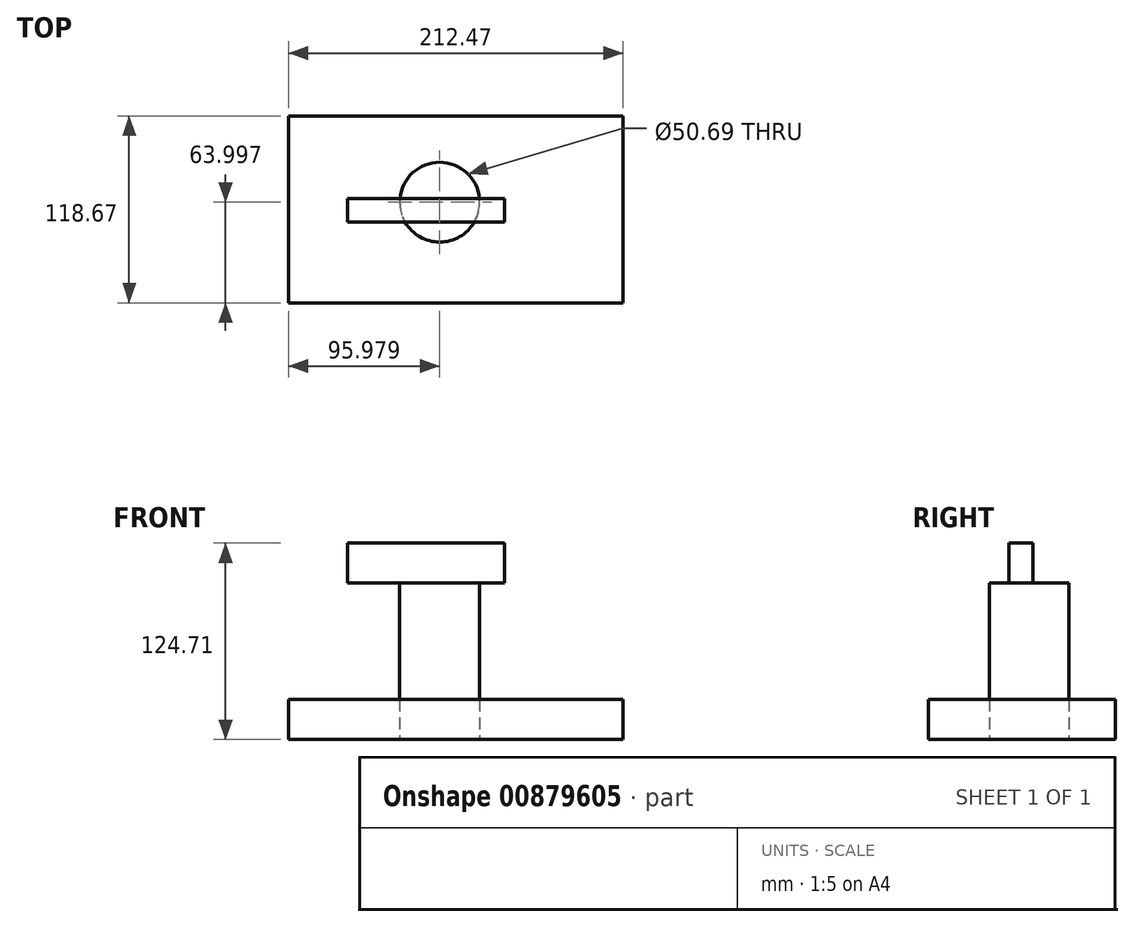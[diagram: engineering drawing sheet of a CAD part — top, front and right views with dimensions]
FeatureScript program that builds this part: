
annotation { "Feature Type Name" : "Feature", "Feature Type Description" : "" }
export const myFeature = defineFeature(function(context is Context, id is Id, definition is map)
    precondition{}
    {
        {
            var Q0;
            Q0=qCreatedBy(makeId("Top.planeOp"),FACE);
            var sketch = newSketch(context, id + "F0", { "sketchPlane" : qUnion([Q0])});
            skLineSegment(sketch, "E0.bottom", {"start": v(-143.27, 59.79) * mm, "end": v(69.2, 59.79) * mm});
            skLineSegment(sketch, "E0.top", {"start": v(-143.27, -58.88) * mm, "end": v(69.2, -58.88) * mm});
            skLineSegment(sketch, "E0.left", {"start": v(-143.27, 59.79) * mm, "end": v(-143.27, -58.88) * mm});
            skLineSegment(sketch, "E0.right", {"start": v(69.2, 59.79) * mm, "end": v(69.2, -58.88) * mm});
            skCircle(sketch, "E1", {"center": v(-47.3, 5.12) * mm, "radius": 25.35 * mm});
            skSolve(sketch);
        }
        {
            var Q0;
            Q0=makeQuery(id+"F0.imprint","IMPRINT",FACE,{"disambiguationData":[TD([[makeQuery(id+"F0.imprint","IMPRINT",EDGE,{"derivedFrom":sQuery(id+"F0.wireOp",EDGE,"E0.bottom")}),-1.0]])]});
            extrude(context, id + "F1", {"entities" : qUnion([Q0]), "depth" : 25.4 * mm, "offsetDistance" : 25.4 * mm});
        }
        {
            var Q0;
            Q0=makeQuery(id+"F1.opExtrude","CAP_FACE",FACE,{"disambiguationData":[OSD([sQuery(id+"F0.wireOp",EDGE,"E0.bottom"),sQuery(id+"F0.wireOp",EDGE,"E0.top"),sQuery(id+"F0.wireOp",EDGE,"E0.left"),sQuery(id+"F0.wireOp",EDGE,"E0.right"),sQuery(id+"F0.wireOp",EDGE,"E1")])],"isStart":false});
            var sketch = newSketch(context, id + "F2", { "sketchPlane" : qUnion([Q0])});
            skCircle(sketch, "E2.0", {"center": v(-47.3, 5.12) * mm, "radius": 25.35 * mm});
            skSolve(sketch);
        }
        {
            var Q0;
            Q0 = qSketchRegion(id + "F2", true);
            extrude(context, id + "F3", {"entities" : qUnion([Q0]), "depth" : 73.9 * mm, "offsetDistance" : 25.4 * mm});
        }
        {
            var Q0;
            Q0=makeQuery(id+"F3.opExtrude","CAP_FACE",FACE,{"disambiguationData":[OSD([sQuery(id+"F2.wireOp",EDGE,"E2.0")])],"isStart":false});
            var sketch = newSketch(context, id + "F4", { "sketchPlane" : qUnion([Q0])});
            skLineSegment(sketch, "E3.bottom", {"start": v(-105.78, 7.41) * mm, "end": v(-6.07, 7.41) * mm});
            skLineSegment(sketch, "E3.top", {"start": v(-105.78, -7.6) * mm, "end": v(-6.07, -7.6) * mm});
            skLineSegment(sketch, "E3.left", {"start": v(-105.78, 7.41) * mm, "end": v(-105.78, -7.6) * mm});
            skLineSegment(sketch, "E3.right", {"start": v(-6.07, 7.41) * mm, "end": v(-6.07, -7.6) * mm});
            skSolve(sketch);
        }
        {
            var Q0;
            Q0 = qSketchRegion(id + "F4", true);
            extrude(context, id + "F5", {"entities" : qUnion([Q0]), "operationType" : NewBodyOperationType.ADD, "depth" : 25.4 * mm, "offsetDistance" : 25.4 * mm});
        }
    });
